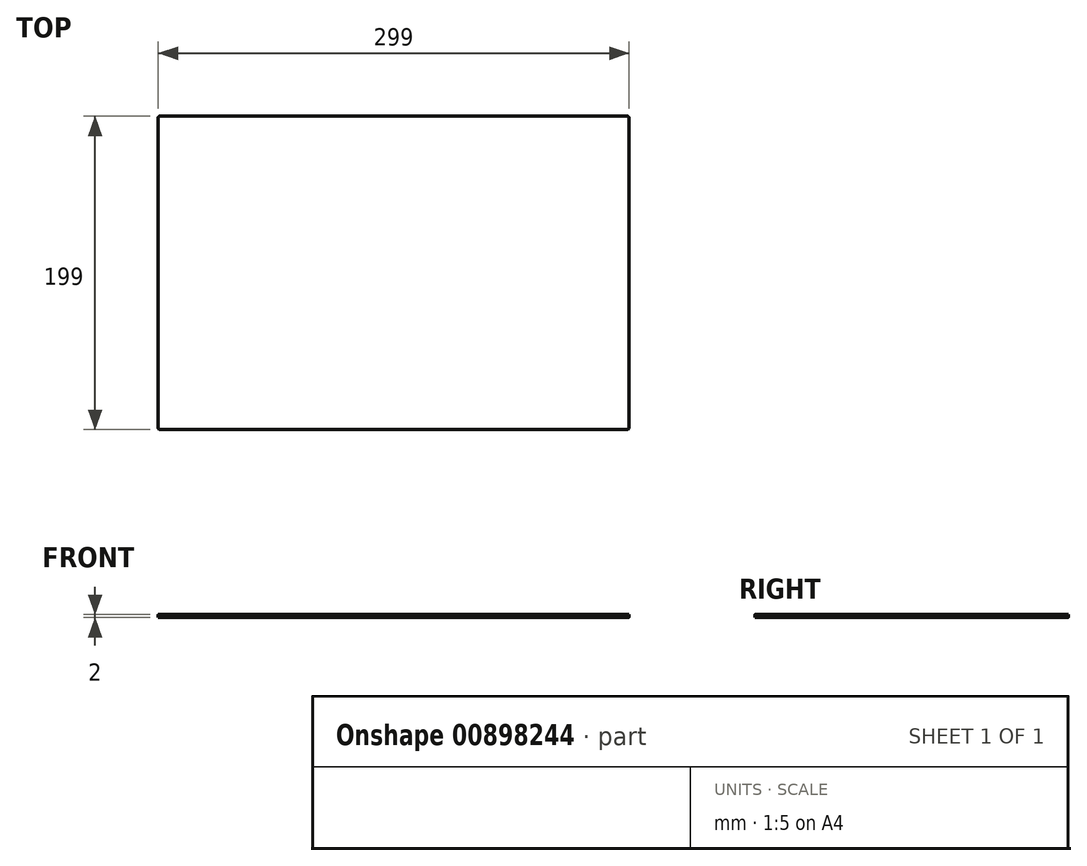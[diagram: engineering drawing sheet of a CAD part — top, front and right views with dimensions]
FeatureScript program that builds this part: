
annotation { "Feature Type Name" : "Feature", "Feature Type Description" : "" }
export const myFeature = defineFeature(function(context is Context, id is Id, definition is map)
    precondition{}
    {
        {
            var Q0;
            Q0=qCreatedBy(makeId("Top.planeOp"),FACE);
            var sketch = newSketch(context, id + "F0", { "sketchPlane" : qUnion([Q0])});
            skLineSegment(sketch, "E0.bottom", {"start": v(148.5, -99.5) * mm, "end": v(-148.5, -99.5) * mm});
            skLineSegment(sketch, "E0.top", {"start": v(148.5, 99.5) * mm, "end": v(-148.5, 99.5) * mm});
            skLineSegment(sketch, "E0.left", {"start": v(149.5, -98.5) * mm, "end": v(149.5, 98.5) * mm});
            skLineSegment(sketch, "E0.right", {"start": v(-149.5, -98.5) * mm, "end": v(-149.5, 98.5) * mm});
            skPoint(sketch, "E0.middle", {"position": v(0, 0) * mm});
            skPoint(sketch, "E1.visualSharp", {"position": v(-149.5, 99.5) * mm});
            skArc(sketch, "E1.filletArc", {"start": v(-148.5, 99.5) * mm, "mid": v(-149.2, 99.2) * mm, "end": v(-149.5, 98.5) * mm});
            skPoint(sketch, "E2.visualSharp", {"position": v(149.5, 99.5) * mm});
            skArc(sketch, "E2.filletArc", {"start": v(149.5, 98.5) * mm, "mid": v(149.2, 99.2) * mm, "end": v(148.5, 99.5) * mm});
            skPoint(sketch, "E3.visualSharp", {"position": v(-149.5, -99.5) * mm});
            skArc(sketch, "E3.filletArc", {"start": v(-149.5, -98.5) * mm, "mid": v(-149.2, -99.2) * mm, "end": v(-148.5, -99.5) * mm});
            skPoint(sketch, "E4.visualSharp", {"position": v(149.5, -99.5) * mm});
            skArc(sketch, "E4.filletArc", {"start": v(148.5, -99.5) * mm, "mid": v(149.2, -99.2) * mm, "end": v(149.5, -98.5) * mm});
            skSolve(sketch);
        }
        {
            var Q0;
            Q0=qSketchRegion(id+"F0",true);
            extrude(context, id + "F1", {"entities" : qUnion([Q0]), "oppositeDirection" : true, "depth" : 2 * mm});
        }
    });
